# Revit family: 201_OKE-_
name_source: partatom
category: Air Terminals
units: mm (PartAtom-declared; Revit-internal decimal feet)

## family parameters
Always vertical = Yes
Cut with Voids When Loaded = No
Part Type = Normal
Room Calculation Point = Yes
Round Connector Dimension = Use Diameter
Shared = No
Work Plane-Based = No

## types (4) — shared parameters
CAT0 = Yes
CL_Location_5000 = 5000 mm  [stored 16.4042 ft]
Description = Wall diffuser
L_ARR = 400 mm  [stored 1.31234 ft]
Manufacturer = Climecon
QmdConnectorList = 201;D
URL = www.climecon.fi
W_ARR = 400 mm  [stored 1.31234 ft]
XRefLineVPlnId = 7453
YRefLineVPlnId = 7456
magiPartTypeId = 201
magiProductFamilyId = OKE-*
zero-valued in all types: CLBTZ, H_ARR, MC_Default_elevation

## per-type parameters (varying)
| type | A | AA | BB | D | RX | X |
| OKE-100 | 230 mm  [stored 0.754593 ft] | 115 mm  [stored 0.377297 ft] | 70 mm  [stored 0.229659 ft] | 100 mm | 38 mm  [stored 0.124672 ft] | 22 mm  [stored 0.0721785 ft] |
| OKE-200 | 440 mm  [stored 1.44357 ft] | 220 mm  [stored 0.721785 ft] | 141 mm  [stored 0.462598 ft] | 200 mm | 68 mm  [stored 0.223097 ft] | 32 mm  [stored 0.104987 ft] |
| OKE-160 | 360 mm  [stored 1.1811 ft] | 180 mm  [stored 0.590551 ft] | 113 mm  [stored 0.370735 ft] | 160 mm | 58 mm  [stored 0.190289 ft] | 32 mm  [stored 0.104987 ft] |
| OKE-125 | 280 mm  [stored 0.918635 ft] | 140 mm  [stored 0.459318 ft] | 89 mm | 125 mm | 47 mm  [stored 0.154199 ft] | 26 mm  [stored 0.0853018 ft] |

note: column(s) folded — value = type name in every type: magiProductCode, magiProductId

note: [stored X ft] marks values corroborated as IEEE doubles in the binary element streams (Revit-internal decimal feet)

## geometry (parser evidence)
native form markers: Sweep x2
no freeform markers — native parametric forms only
